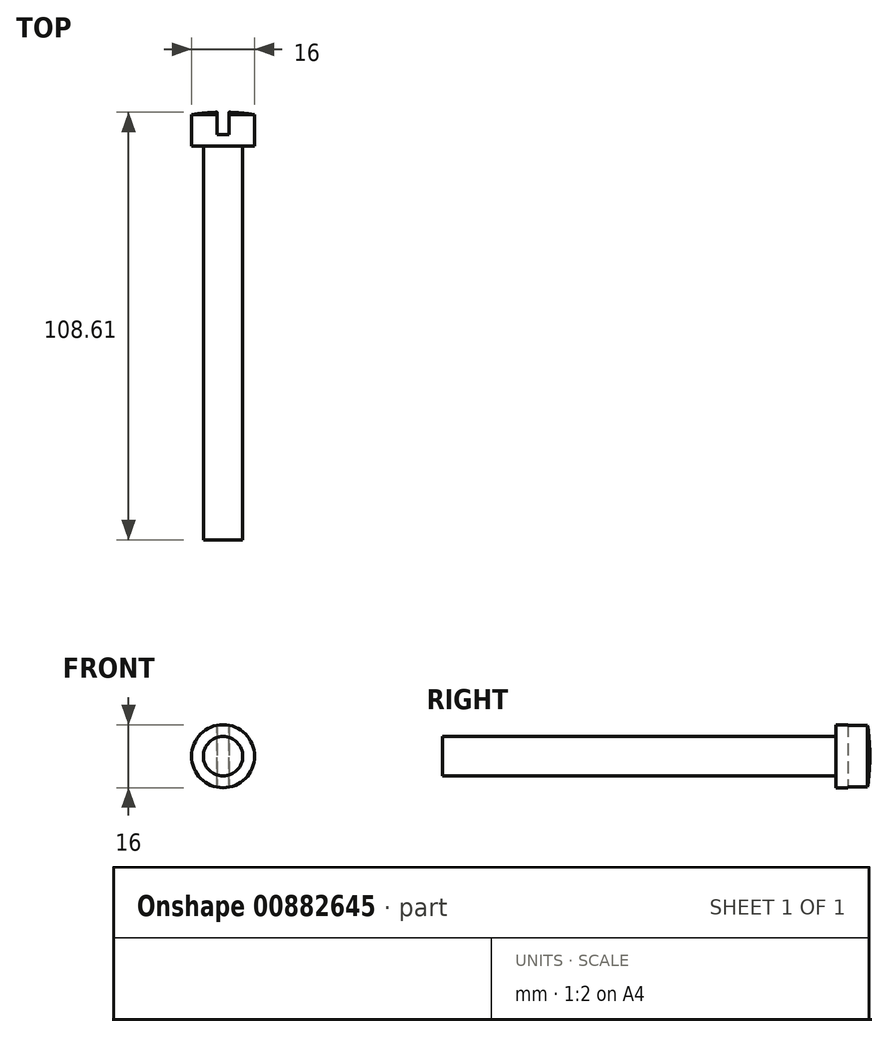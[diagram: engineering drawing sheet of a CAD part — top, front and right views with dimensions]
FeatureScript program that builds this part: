
annotation { "Feature Type Name" : "Feature", "Feature Type Description" : "" }
export const myFeature = defineFeature(function(context is Context, id is Id, definition is map)
    precondition{}
    {
        {
            var Q0;
            Q0=qCreatedBy(makeId("Right.planeOp"),FACE);
            var sketch = newSketch(context, id + "F0", { "sketchPlane" : qUnion([Q0])});
            skLineSegment(sketch, "E0", {"start": v(0, 8) * mm, "end": v(-8, 8) * mm});
            skLineSegment(sketch, "E1", {"start": v(-8, 8) * mm, "end": v(-8, 5) * mm});
            skLineSegment(sketch, "E2", {"start": v(-8, 5) * mm, "end": v(-108, 5) * mm});
            skLineSegment(sketch, "E3", {"start": v(0.65, 0) * mm, "end": v(-108, 0) * mm});
            skLineSegment(sketch, "E4", {"start": v(-108, 0) * mm, "end": v(-108, 5) * mm});
            skArc(sketch, "E5", {"start": v(0.65, 0) * mm, "mid": v(0.45, 4.01) * mm, "end": v(0, 8) * mm});
            skSolve(sketch);
        }
        {
            var Q0;
            Q0 = qSketchRegion(id + "F0", true);
            var Q1;
            Q1=sQuery(id+"F0.wireOp",EDGE,"E3");
            revolve(context, id + "F1", {"surfaceOperationType" : NewSurfaceOperationType.NEW, "entities" : qUnion([Q0]), "axis" : qUnion([Q1]), "revolveType" : RevolveType.FULL});
        }
        {
            var Q0;
            Q0=qCreatedBy(makeId("Front.planeOp"),FACE);
            var sketch = newSketch(context, id + "F2", { "sketchPlane" : qUnion([Q0])});
            skLineSegment(sketch, "E6.bottom", {"start": v(-1.5, 10.14) * mm, "end": v(1.5, 10.14) * mm});
            skLineSegment(sketch, "E6.top", {"start": v(-1.5, -14.52) * mm, "end": v(1.5, -14.52) * mm});
            skLineSegment(sketch, "E6.left", {"start": v(-1.5, 10.14) * mm, "end": v(-1.5, -14.52) * mm});
            skLineSegment(sketch, "E6.right", {"start": v(1.5, 10.14) * mm, "end": v(1.5, -14.52) * mm});
            skSolve(sketch);
        }
        {
            var Q0;
            Q0 = qSketchRegion(id + "F2", true);
            extrude(context, id + "F3", {"entities" : qUnion([Q0]), "operationType" : NewBodyOperationType.REMOVE, "oppositeDirection" : true, "depth" : 25 * mm, "offsetDistance" : 25 * mm, "hasSecondDirection" : true, "secondDirectionOppositeDirection" : false, "secondDirectionDepth" : 5 * mm});
        }
    });
